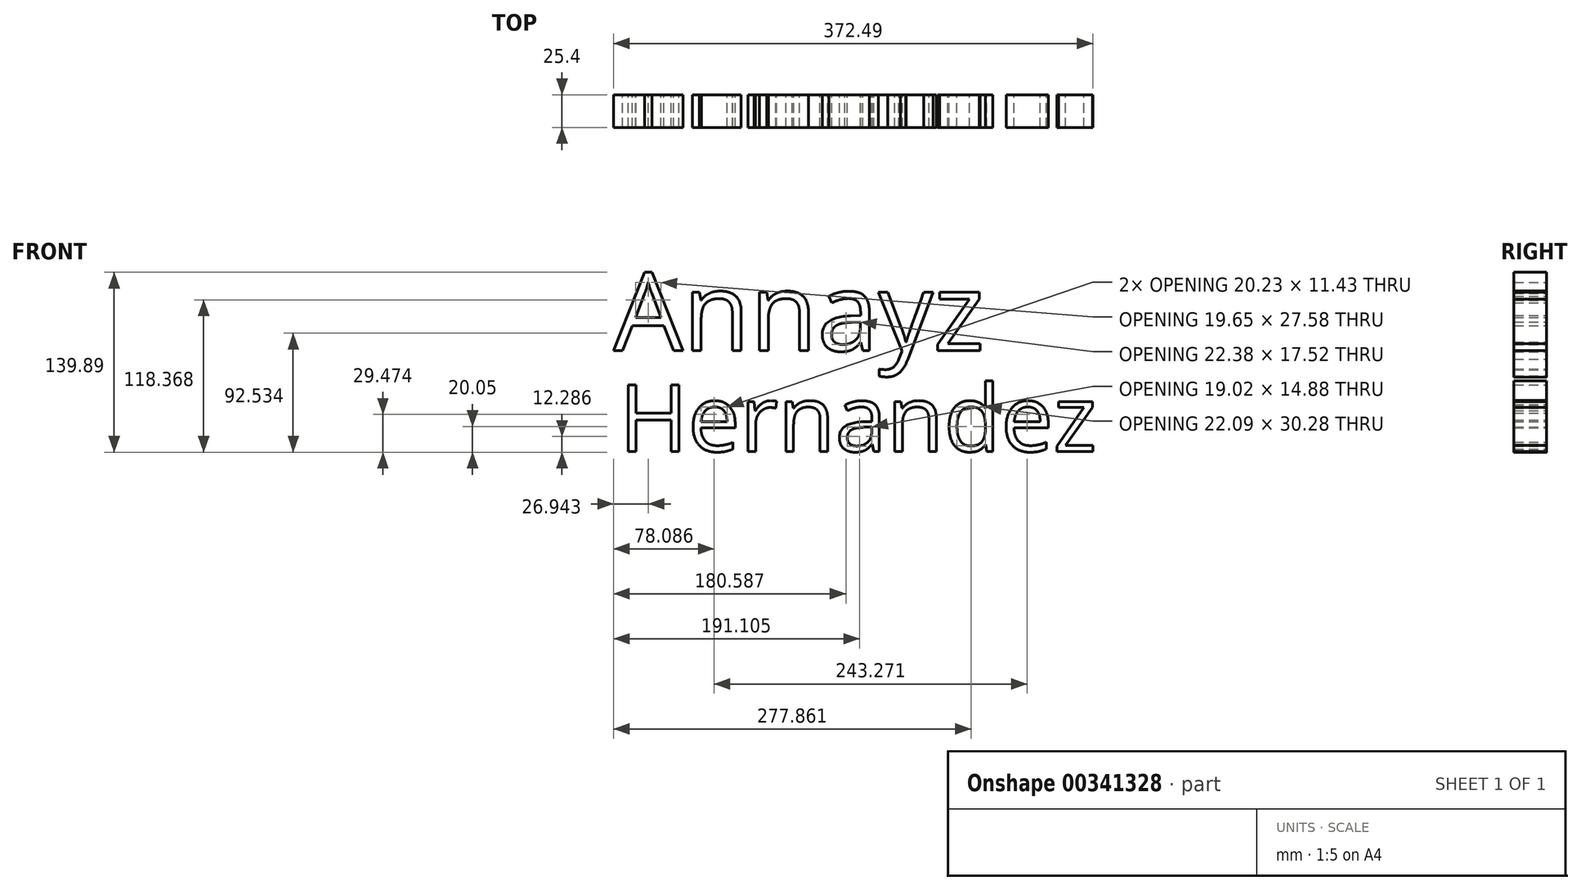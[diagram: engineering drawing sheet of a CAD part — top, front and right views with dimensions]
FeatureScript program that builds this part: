
annotation { "Feature Type Name" : "Feature", "Feature Type Description" : "" }
export const myFeature = defineFeature(function(context is Context, id is Id, definition is map)
    precondition{}
    {
        {
            var Q0;
            Q0=qCreatedBy(makeId("Front.planeOp"),FACE);
            var sketch = newSketch(context, id + "F0", { "sketchPlane" : qUnion([Q0])});
            skText(sketch, "E0", { "text": "Annayz", "fontName": "OpenSans-Regular.ttf"});
            skText(sketch, "E1", { "text": "Hernandez", "fontName": "OpenSans-Regular.ttf"});
            const initialGuessF0  = {"E0": [-0.13074, 0, 1, 0, 0.06125], "E1": [-0.12636, -0.0782, 1, 0, 0.05204]};
            skSetInitialGuess(sketch, initialGuessF0);
            skSolve(sketch);
        }
        {
            var Q0;
            Q0 = qSketchRegion(id + "F0", true);
            extrude(context, id + "F1", {"entities" : qUnion([Q0]), "depth" : 25.4 * mm});
        }
    });
